# Revit family: E_Cable Tray Support_MEPcontent_OBO Bettermann_Bracket MWA FS
name_source: partatom
category: Cable Tray Fittings
revit_build: Autodesk Revit MEP 2015 (Build: 20140606_1530(x64)
units: mm (PartAtom-declared; Revit-internal decimal feet)

## types (4) — shared parameters
Article Description = Wall Bracket
Description = Wall Bracket
EMCS Version = 2.0
ETIM Article Class = EC000022
Family Version = 10.14
Gray = Color RGB 189-187-185
IFCExportAs = IfcCableCarrierFittingType
IFCExportType = NOTDEFINED
MEPcontent Class = CABLE_TRAY_SUPPORT
Manufacturer = OBO BETTERMANN
Manufacturer URL = http://catalog4.obo-bettermann.com
Product Line = OBO BETTERMANN CableTrays
Revit Version = 2015
URL = www.stabiplan.com

## per-type parameters (varying)
| type | Depth | Front Height | GTIN | Height | Height 1 | Manufacturer Art. No. | Width | Width 1 |
| MWA 12 11S FS | 32.5 mm  [stored 0.106627 ft] | 13.25 mm  [stored 0.0434711 ft] | 4012196636853 | 53 mm | 53 mm  [stored 0.173885 ft] | 6424716 | 110 mm | 110 mm  [stored 0.360892 ft] |
| MWA 12 21S FS | 32.5 mm  [stored 0.106627 ft] | 16.25 mm  [stored 0.0533136 ft] | 4012196636976 | 65 mm | 65 mm  [stored 0.213255 ft] | 6424732 | 210 mm | 210 mm  [stored 0.688976 ft] |
| MWA 12 31S FS | 38 mm  [stored 0.124672 ft] | 18.75 mm | 4012196637034 | 75 mm | 75 mm | 6424740 | 310 mm | 310 mm  [stored 1.01706 ft] |
| MWA 12 41S FS | 38 mm  [stored 0.124672 ft] | 20.75 mm  [stored 0.0680774 ft] | 4012196637096 | 83 mm | 83 mm  [stored 0.27231 ft] | 6424759 | 410 mm | 410 mm  [stored 1.34514 ft] |

note: column(s) folded — value = type name in every type: Article Type, Model

note: [stored X ft] marks values corroborated as IEEE doubles in the binary element streams (Revit-internal decimal feet)

## geometry (parser evidence)
native form markers: Blend x4, Sweep x3
no freeform markers — native parametric forms only
